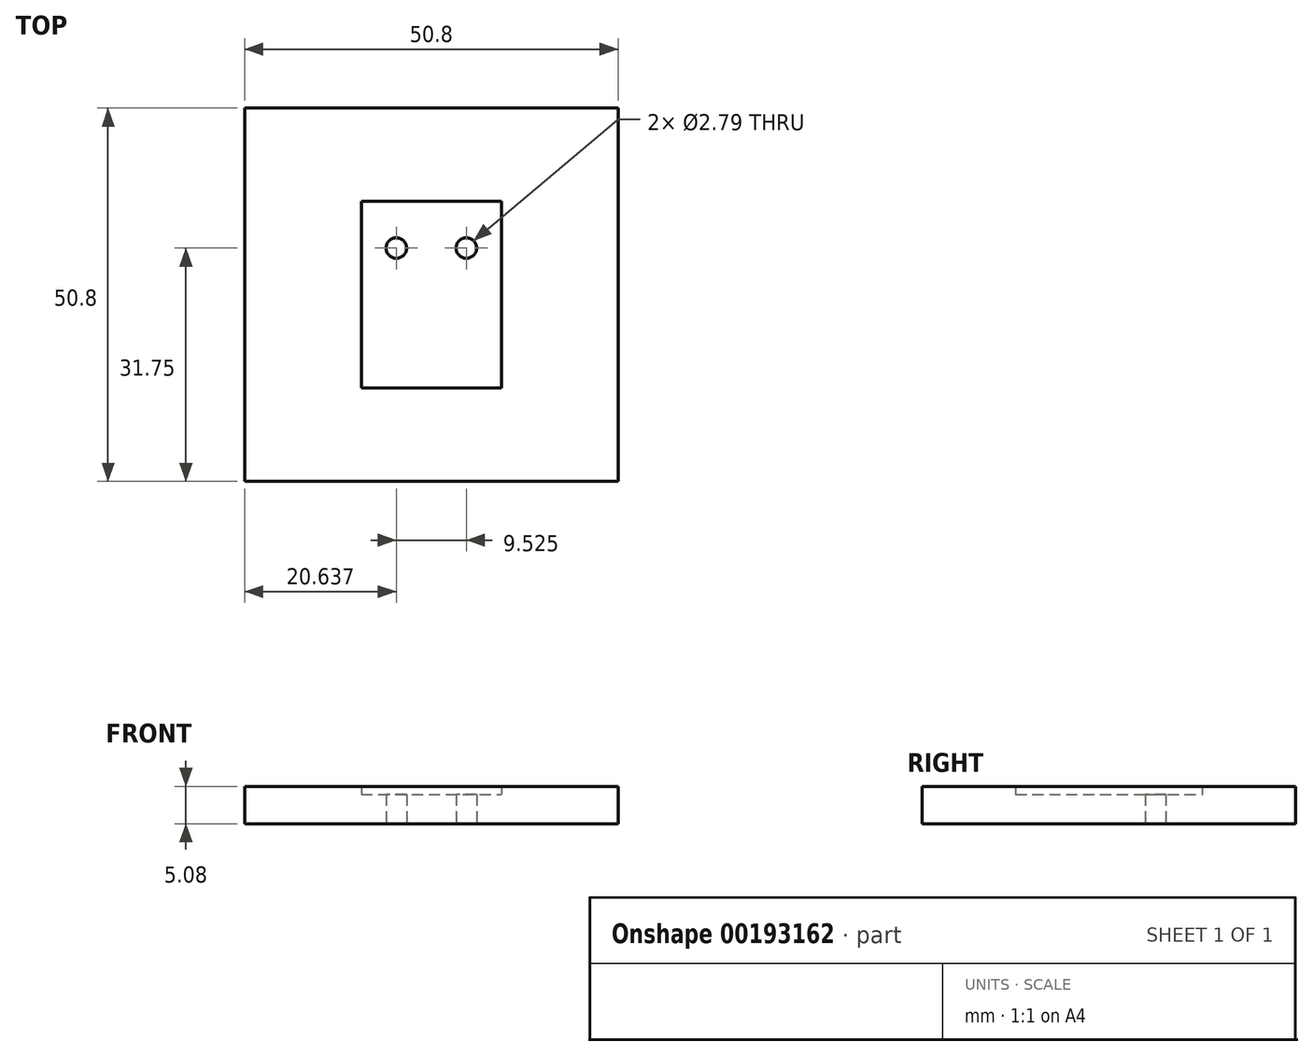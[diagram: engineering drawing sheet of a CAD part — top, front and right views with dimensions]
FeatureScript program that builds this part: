
annotation { "Feature Type Name" : "Feature", "Feature Type Description" : "" }
export const myFeature = defineFeature(function(context is Context, id is Id, definition is map)
    precondition{}
    {
        {
            var Q0;
            Q0=qCreatedBy(makeId("Top.planeOp"),FACE);
            var sketch = newSketch(context, id + "F0", { "sketchPlane" : qUnion([Q0])});
            skLineSegment(sketch, "E0.bottom", {"start": v(-25.4, -25.4) * mm, "end": v(25.4, -25.4) * mm});
            skLineSegment(sketch, "E0.top", {"start": v(-25.4, 25.4) * mm, "end": v(25.4, 25.4) * mm});
            skLineSegment(sketch, "E0.left", {"start": v(-25.4, -25.4) * mm, "end": v(-25.4, 25.4) * mm});
            skLineSegment(sketch, "E0.right", {"start": v(25.4, -25.4) * mm, "end": v(25.4, 25.4) * mm});
            skPoint(sketch, "E0.middle", {"position": v(0, 0) * mm});
            skLineSegment(sketch, "E1.bottom", {"start": v(-9.52, -12.7) * mm, "end": v(9.53, -12.7) * mm});
            skLineSegment(sketch, "E1.top", {"start": v(-9.53, 12.7) * mm, "end": v(9.52, 12.7) * mm});
            skLineSegment(sketch, "E1.left", {"start": v(-9.52, -12.7) * mm, "end": v(-9.53, 12.7) * mm});
            skLineSegment(sketch, "E1.right", {"start": v(9.53, -12.7) * mm, "end": v(9.52, 12.7) * mm});
            skLineSegment(sketch, "E2.bottom", {"start": v(-2.2, -3.7) * mm, "end": v(2.2, -3.7) * mm});
            skLineSegment(sketch, "E2.top", {"start": v(-2.2, 3.7) * mm, "end": v(2.2, 3.7) * mm});
            skLineSegment(sketch, "E2.left", {"start": v(-2.2, -3.7) * mm, "end": v(-2.2, 3.7) * mm});
            skLineSegment(sketch, "E2.right", {"start": v(2.2, -3.7) * mm, "end": v(2.2, 3.7) * mm});
            skLineSegment(sketch, "E3", {"start": v(-9.53, 0) * mm, "end": v(9.53, 0) * mm, "construction": true});
            skLineSegment(sketch, "E4", {"start": v(0, 12.7) * mm, "end": v(0, 0) * mm, "construction": true});
            skLineSegment(sketch, "E5", {"start": v(-9.52, 6.35) * mm, "end": v(9.52, 6.35) * mm, "construction": true});
            skPoint(sketch, "E6.orphan", {"position": v(0, 6.35) * mm});
            skCircle(sketch, "E7", {"center": v(-4.76, 6.35) * mm, "radius": 1.4 * mm});
            skCircle(sketch, "E8.MirrorC", {"center": v(4.76, 6.35) * mm, "radius": 1.4 * mm});
            skSolve(sketch);
        }
        {
            var Q0;
            Q0=makeQuery(id+"F0.imprint","IMPRINT",FACE,{"disambiguationData":[TD([[makeQuery(id+"F0.imprint","IMPRINT",EDGE,{"derivedFrom":sQuery(id+"F0.wireOp",EDGE,"E0.bottom")}),1.0]])]});
            extrude(context, id + "F1", {"entities" : qUnion([Q0]), "depth" : 5.08 * mm});
        }
        {
            var Q0;
            Q0=makeQuery(id+"F0.imprint","IMPRINT",FACE,{"disambiguationData":[TD([[makeQuery(id+"F0.imprint","IMPRINT",EDGE,{"derivedFrom":sQuery(id+"F0.wireOp",EDGE,"E1.bottom")}),1.0]])]});
            var Q1;
            Q1=makeQuery(id+"F0.imprint","IMPRINT",FACE,{"disambiguationData":[TD([[makeQuery(id+"F0.imprint","IMPRINT",EDGE,{"derivedFrom":sQuery(id+"F0.wireOp",EDGE,"E2.bottom")}),1.0]])]});
            extrude(context, id + "F2", {"entities" : qUnion([Q0, Q1]), "operationType" : NewBodyOperationType.ADD, "depth" : 3.97 * mm});
        }
    });
